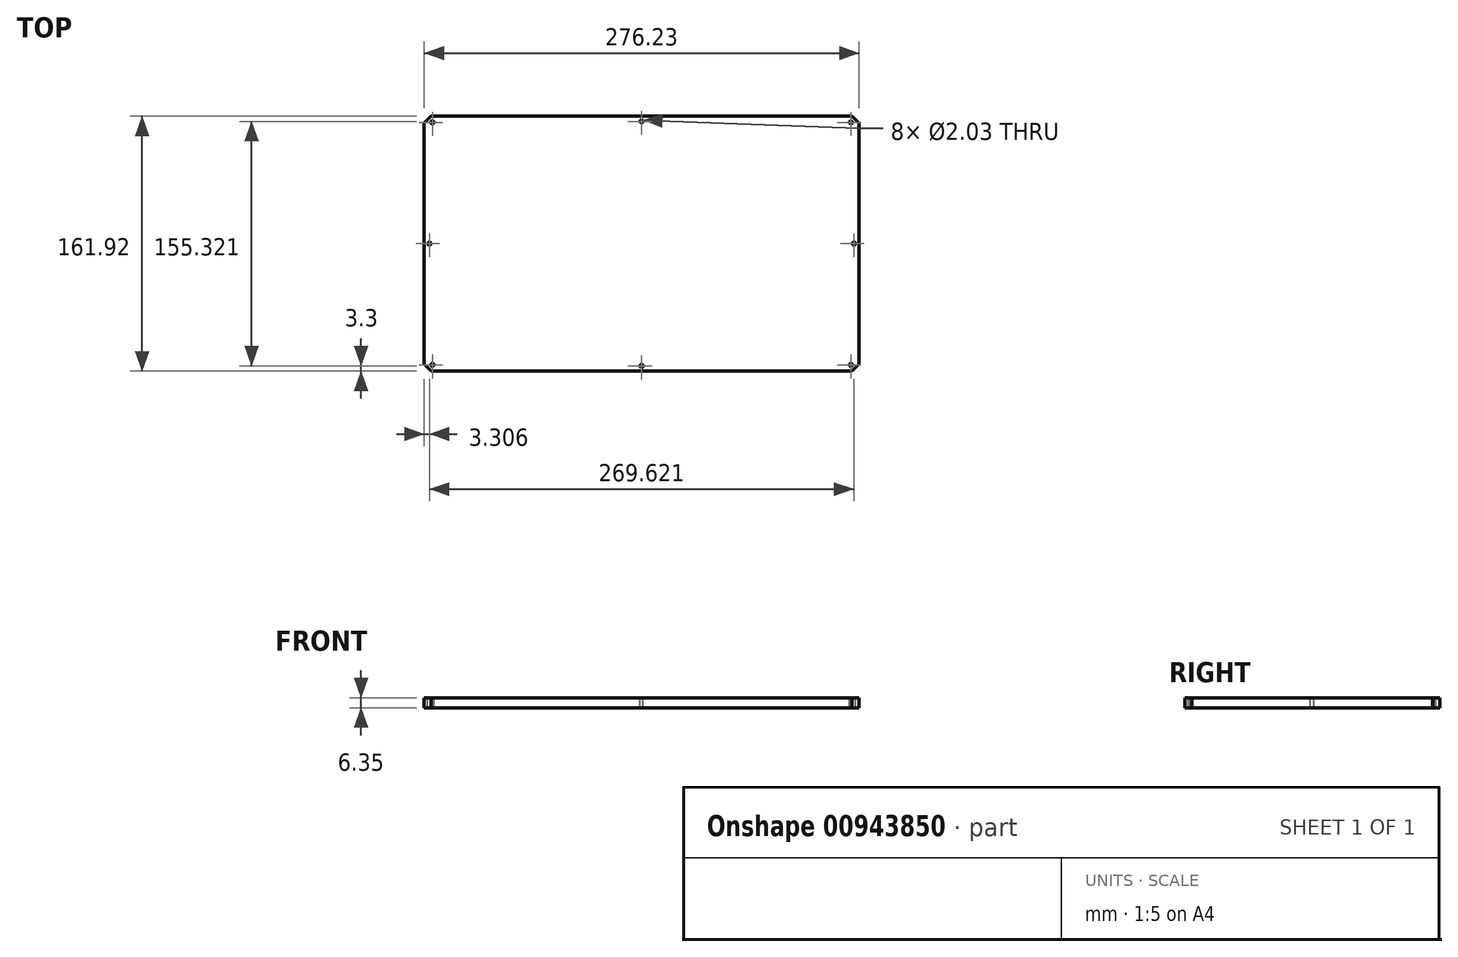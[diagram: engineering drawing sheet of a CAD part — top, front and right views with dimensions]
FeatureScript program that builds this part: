
annotation { "Feature Type Name" : "Feature", "Feature Type Description" : "" }
export const myFeature = defineFeature(function(context is Context, id is Id, definition is map)
    precondition{}
    {
        {
            var Q0;
            Q0=qCreatedBy(makeId("Top.planeOp"),FACE);
            var sketch = newSketch(context, id + "F0", { "sketchPlane" : qUnion([Q0])});
            skLineSegment(sketch, "E0.bottom", {"start": v(-135.03, 71.73) * mm, "end": v(141.2, 71.73) * mm});
            skLineSegment(sketch, "E0.top", {"start": v(-135.03, -90.2) * mm, "end": v(141.2, -90.2) * mm});
            skLineSegment(sketch, "E0.left", {"start": v(-135.03, 71.73) * mm, "end": v(-135.03, -90.2) * mm});
            skLineSegment(sketch, "E0.right", {"start": v(141.2, 71.73) * mm, "end": v(141.2, -90.2) * mm});
            skSolve(sketch);
        }
        {
            var Q0;
            Q0 = qSketchRegion(id + "F0", true);
            extrude(context, id + "F1", {"entities" : qUnion([Q0]), "depth" : 6.35 * mm, "offsetDistance" : 25.4 * mm});
        }
        {
            var Q0;
            Q0=makeQuery(id+"F1.opExtrude","SWEPT_EDGE",EDGE,{"disambiguationData":[OSD([sQuery(id+"F0.wireOp",EDGE,"E0.bottom"),sQuery(id+"F0.wireOp",EDGE,"E0.left")])]});
            var Q1;
            Q1=makeQuery(id+"F1.opExtrude","SWEPT_EDGE",EDGE,{"disambiguationData":[OSD([sQuery(id+"F0.wireOp",EDGE,"E0.bottom"),sQuery(id+"F0.wireOp",EDGE,"E0.right")])]});
            var Q2;
            Q2=makeQuery(id+"F1.opExtrude","SWEPT_EDGE",EDGE,{"disambiguationData":[OSD([sQuery(id+"F0.wireOp",EDGE,"E0.top"),sQuery(id+"F0.wireOp",EDGE,"E0.right")])]});
            var Q3;
            Q3=makeQuery(id+"F1.opExtrude","SWEPT_EDGE",EDGE,{"disambiguationData":[OSD([sQuery(id+"F0.wireOp",EDGE,"E0.top"),sQuery(id+"F0.wireOp",EDGE,"E0.left")])]});
            chamfer(context, id + "F2", {"entities" : qUnion([Q0, Q1, Q2, Q3]), "width" : 4.47 * mm, "tangentPropagation" : true});
        }
        {
            var Q0;
            Q0=makeQuery(id+"F1.opExtrude","CAP_FACE",FACE,{"disambiguationData":[OSD([sQuery(id+"F0.wireOp",EDGE,"E0.bottom"),sQuery(id+"F0.wireOp",EDGE,"E0.top"),sQuery(id+"F0.wireOp",EDGE,"E0.left"),sQuery(id+"F0.wireOp",EDGE,"E0.right")])],"isStart":false});
            var sketch = newSketch(context, id + "F3", { "sketchPlane" : qUnion([Q0])});
            skLineSegment(sketch, "E1", {"start": v(-135.03, -9.23) * mm, "end": v(141.2, -9.23) * mm, "construction": true});
            skLineSegment(sketch, "E2", {"start": v(3.09, 71.73) * mm, "end": v(3.09, -90.2) * mm, "construction": true});
            skCircle(sketch, "E3", {"center": v(-131.72, -9.23) * mm, "radius": 1.02 * mm});
            skCircle(sketch, "E4", {"center": v(3.09, -86.89) * mm, "radius": 1.02 * mm});
            skCircle(sketch, "E5", {"center": v(3.09, 68.43) * mm, "radius": 1.02 * mm});
            skLineSegment(sketch, "E6", {"start": v(-132.8, 69.5) * mm, "end": v(138.96, -87.96) * mm, "construction": true});
            skLineSegment(sketch, "E7", {"start": v(138.96, 69.5) * mm, "end": v(-132.8, -87.96) * mm, "construction": true});
            skCircle(sketch, "E8", {"center": v(-129.83, 67.79) * mm, "radius": 1.02 * mm});
            skCircle(sketch, "E9.MirrorC", {"center": v(-129.83, -86.24) * mm, "radius": 1.02 * mm});
            skCircle(sketch, "E10.MirrorC", {"center": v(136, -86.24) * mm, "radius": 1.02 * mm});
            skCircle(sketch, "E11.MirrorC", {"center": v(137.9, -9.23) * mm, "radius": 1.02 * mm});
            skCircle(sketch, "E12.MirrorC", {"center": v(136, 67.79) * mm, "radius": 1.02 * mm});
            skSolve(sketch);
        }
        {
            var Q0;
            Q0 = qSketchRegion(id + "F3", true);
            extrude(context, id + "F4", {"entities" : qUnion([Q0]), "operationType" : NewBodyOperationType.REMOVE, "endBound" : BoundingType.THROUGH_ALL, "oppositeDirection" : true, "depth" : 25.4 * mm, "offsetDistance" : 25.4 * mm});
        }
    });
